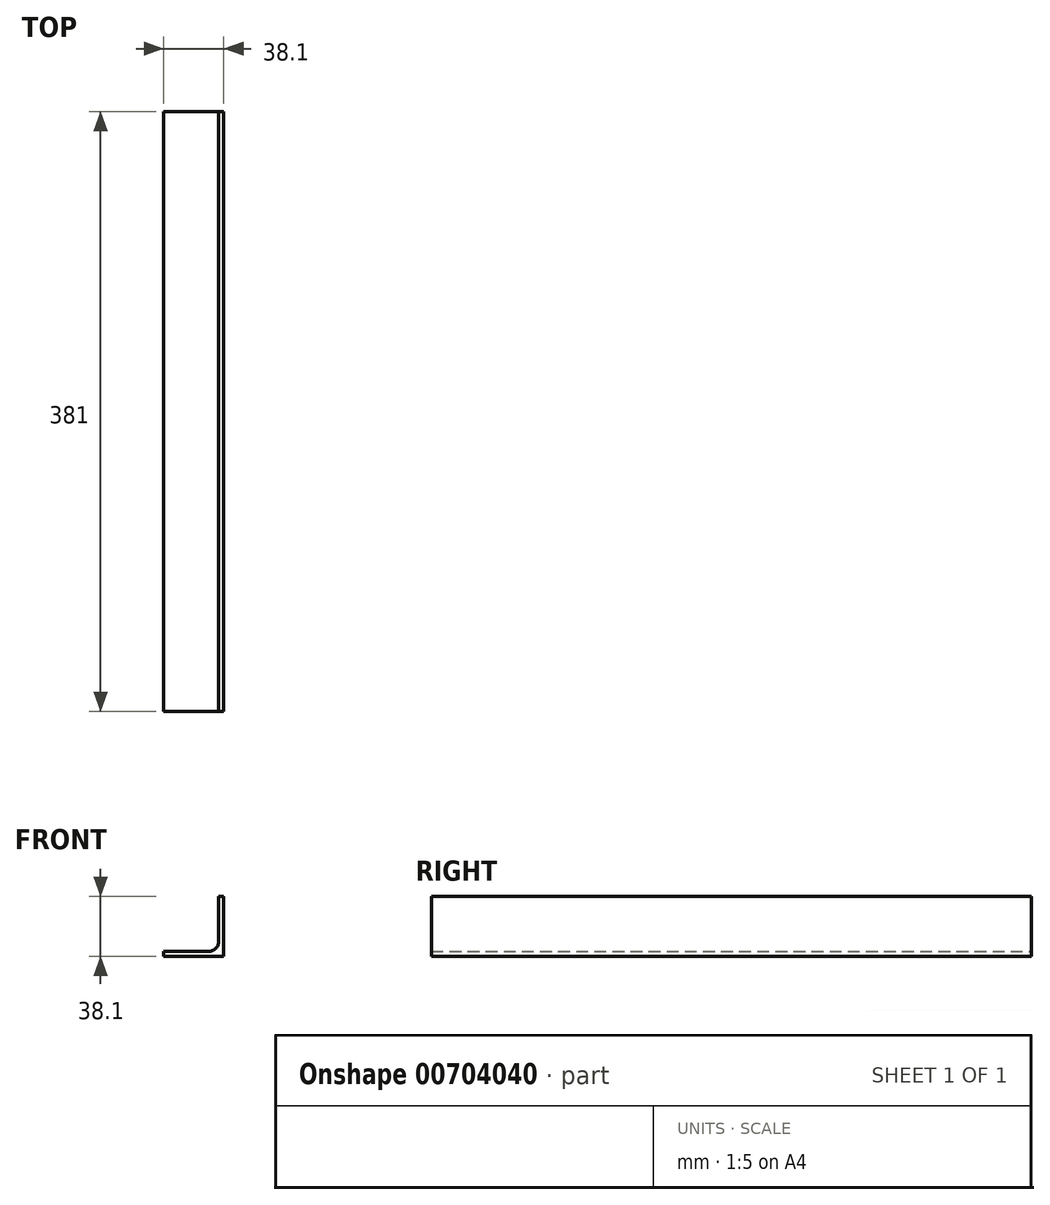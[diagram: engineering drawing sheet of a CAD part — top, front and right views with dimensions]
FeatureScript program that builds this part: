
annotation { "Feature Type Name" : "Feature", "Feature Type Description" : "" }
export const myFeature = defineFeature(function(context is Context, id is Id, definition is map)
    precondition{}
    {
        {
            var Q0;
            Q0=qCreatedBy(makeId("Front.planeOp"),FACE);
            var sketch = newSketch(context, id + "F0", { "sketchPlane" : qUnion([Q0])});
            skLineSegment(sketch, "E0.bottom", {"start": v(0, 0) * mm, "end": v(-38.1, 0) * mm});
            skLineSegment(sketch, "E0.top", {"start": v(-9.53, 3.18) * mm, "end": v(-38.1, 3.17) * mm});
            skLineSegment(sketch, "E0.left", {"start": v(0, 0) * mm, "end": v(0, 5.69) * mm});
            skLineSegment(sketch, "E0.right", {"start": v(-38.1, 0) * mm, "end": v(-38.1, 0) * mm});
            skLineSegment(sketch, "E1.bottom", {"start": v(0, 0) * mm, "end": v(-5.12, 0) * mm});
            skLineSegment(sketch, "E1.top", {"start": v(0, 38.1) * mm, "end": v(0, 38.1) * mm});
            skLineSegment(sketch, "E1.left", {"start": v(0, 0) * mm, "end": v(0, 38.1) * mm});
            skLineSegment(sketch, "E1.right", {"start": v(-3.18, 9.53) * mm, "end": v(-3.18, 38.1) * mm});
            skArc(sketch, "E2.filletArc", {"start": v(-9.53, 3.18) * mm, "mid": v(-5.03, 5.03) * mm, "end": v(-3.18, 9.53) * mm});
            skPoint(sketch, "E3.visualSharp", {"position": v(-3.18, 38.1) * mm});
            skPoint(sketch, "E4.visualSharp", {"position": v(-38.1, 3.17) * mm});
            skLineSegment(sketch, "E5", {"start": v(-38.1, 3.17) * mm, "end": v(-38.1, 0) * mm});
            skLineSegment(sketch, "E6", {"start": v(0, 38.1) * mm, "end": v(-3.18, 38.1) * mm});
            skSolve(sketch);
        }
        {
            var Q0;
            Q0=qSketchRegion(id+"F0",true);
            extrude(context, id + "F1", {"entities" : qUnion([Q0]), "depth" : 381 * mm});
        }
    });
